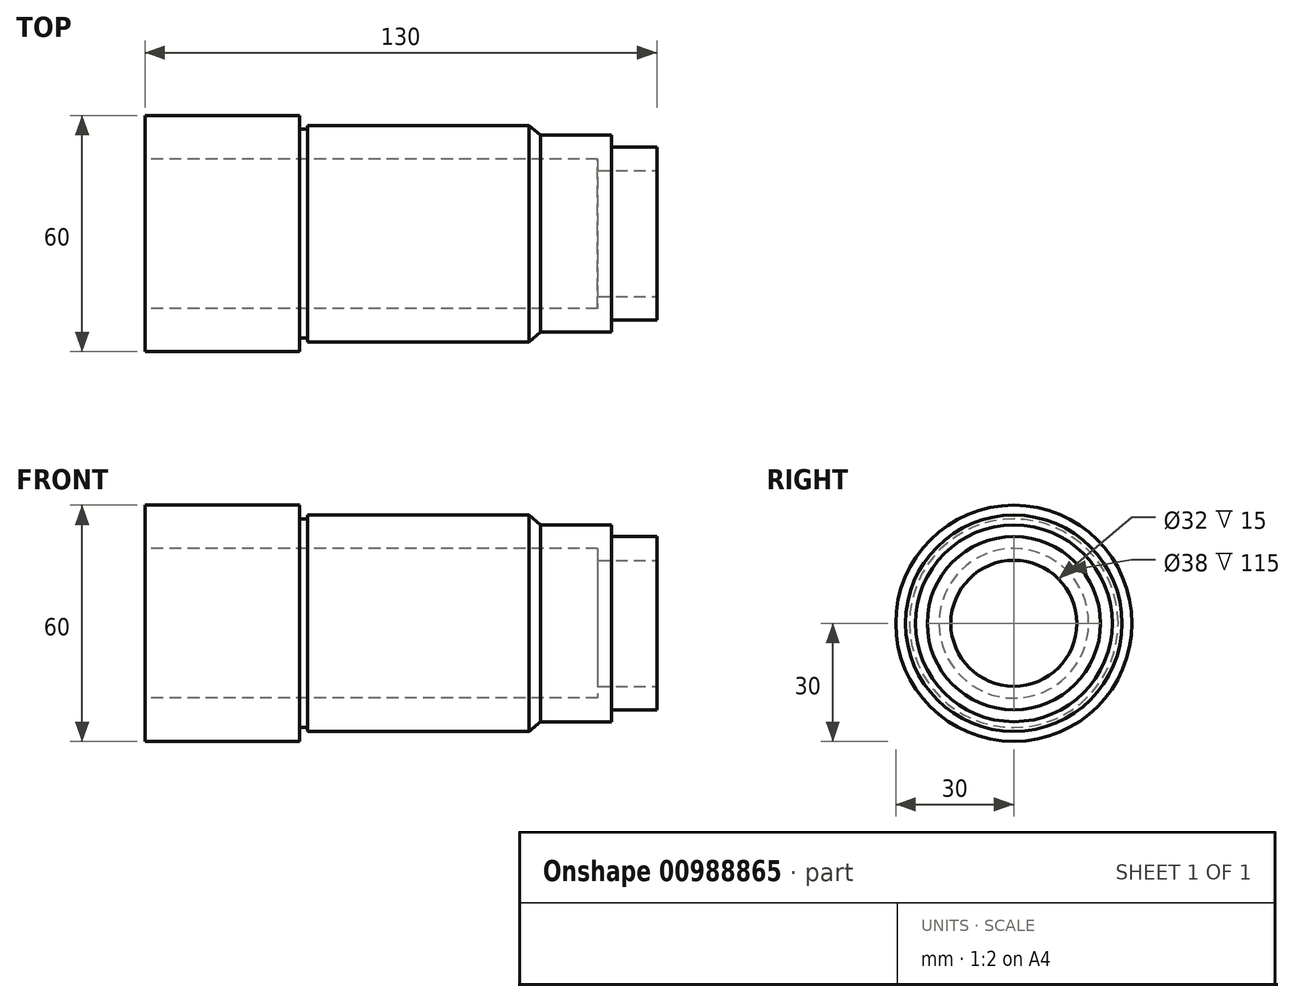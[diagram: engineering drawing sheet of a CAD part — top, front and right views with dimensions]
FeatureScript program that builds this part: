
annotation { "Feature Type Name" : "Feature", "Feature Type Description" : "" }
export const myFeature = defineFeature(function(context is Context, id is Id, definition is map)
    precondition{}
    {
        {
            var Q0;
            Q0=qCreatedBy(makeId("Front.planeOp"),FACE);
            var sketch = newSketch(context, id + "F0", { "sketchPlane" : qUnion([Q0])});
            skLineSegment(sketch, "E0", {"start": v(-65, 0) * mm, "end": v(-65, 30) * mm});
            skLineSegment(sketch, "E1", {"start": v(-65, 30) * mm, "end": v(-25.75, 30) * mm});
            skLineSegment(sketch, "E2", {"start": v(-25.75, 30) * mm, "end": v(-25.75, 26.5) * mm});
            skLineSegment(sketch, "E3", {"start": v(-25.75, 26.5) * mm, "end": v(-23.75, 26.5) * mm});
            skLineSegment(sketch, "E4", {"start": v(35.5, 25) * mm, "end": v(53.5, 25) * mm});
            skLineSegment(sketch, "E5", {"start": v(53.5, 25) * mm, "end": v(53.5, 22) * mm});
            skLineSegment(sketch, "E6", {"start": v(53.5, 22) * mm, "end": v(65, 22) * mm});
            skLineSegment(sketch, "E7", {"start": v(65, 22) * mm, "end": v(65, 0) * mm});
            skLineSegment(sketch, "E8", {"start": v(65, 0) * mm, "end": v(-65, 0) * mm});
            skLineSegment(sketch, "E9", {"start": v(-23.75, 26.5) * mm, "end": v(-23.75, 27.5) * mm});
            skLineSegment(sketch, "E10", {"start": v(-23.75, 27.5) * mm, "end": v(32.5, 27.5) * mm});
            skLineSegment(sketch, "E11", {"start": v(32.5, 27.5) * mm, "end": v(35.5, 25) * mm});
            skSolve(sketch);
        }
        {
            var Q0;
            Q0=makeQuery(id+"F0.imprint","IMPRINT",FACE,{"disambiguationData":[TD([[makeQuery(id+"F0.imprint","IMPRINT",EDGE,{"derivedFrom":sQuery(id+"F0.wireOp",EDGE,"E0")}),-1.0]])]});
            var Q1;
            Q1=sQuery(id+"F0.wireOp",EDGE,"E8");
            revolve(context, id + "F1", {"surfaceOperationType" : NewSurfaceOperationType.NEW, "entities" : qUnion([Q0]), "axis" : qUnion([Q1]), "revolveType" : RevolveType.FULL});
        }
        {
            var Q0;
            Q0=makeQuery(id+"F1.opRevolve","SWEPT_FACE",FACE,{"disambiguationData":[OSD([sQuery(id+"F0.wireOp",EDGE,"E7")])]});
            var sketch = newSketch(context, id + "F2", { "sketchPlane" : qUnion([Q0])});
            skCircle(sketch, "E12", {"center": v(0, 0) * mm, "radius": 16 * mm});
            skSolve(sketch);
        }
        {
            var Q0;
            Q0 = qSketchRegion(id + "F2", true);
            extrude(context, id + "F3", {"entities" : qUnion([Q0]), "operationType" : NewBodyOperationType.REMOVE, "endBound" : BoundingType.UP_TO_NEXT, "oppositeDirection" : true, "depth" : 25 * mm, "offsetDistance" : 25 * mm});
        }
        {
            var Q0;
            Q0=makeQuery(id+"F1.opRevolve","SWEPT_FACE",FACE,{"disambiguationData":[OSD([sQuery(id+"F0.wireOp",EDGE,"E0")])]});
            var sketch = newSketch(context, id + "F4", { "sketchPlane" : qUnion([Q0])});
            skCircle(sketch, "E13", {"center": v(0, 0) * mm, "radius": 19 * mm});
            skSolve(sketch);
        }
        {
            var Q0;
            Q0 = qSketchRegion(id + "F4", true);
            extrude(context, id + "F5", {"entities" : qUnion([Q0]), "operationType" : NewBodyOperationType.REMOVE, "oppositeDirection" : true, "depth" : 115 * mm, "offsetDistance" : 25 * mm});
        }
    });
